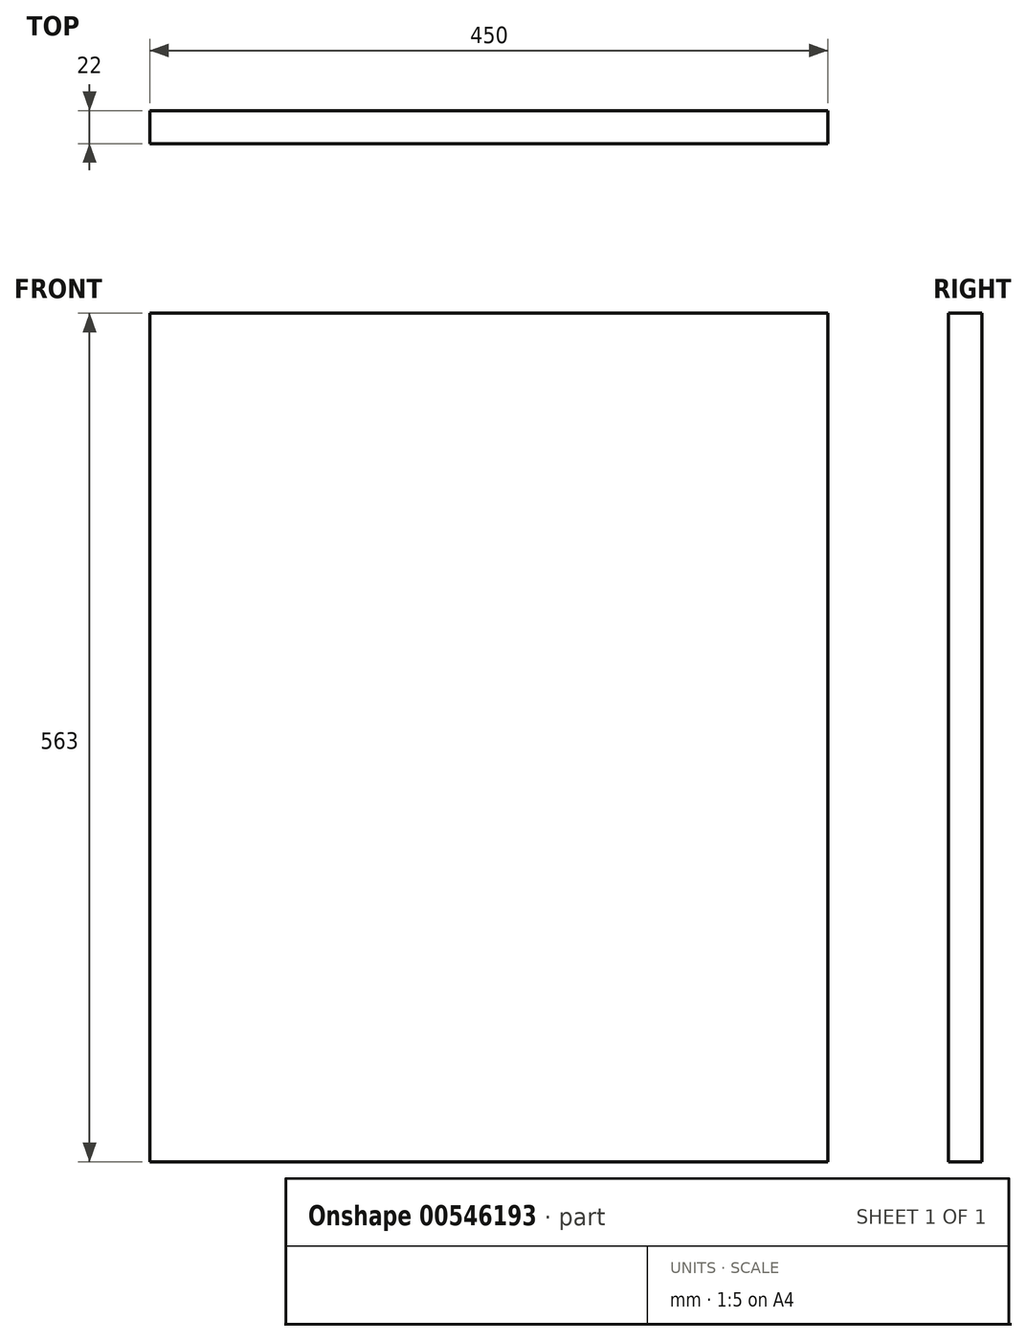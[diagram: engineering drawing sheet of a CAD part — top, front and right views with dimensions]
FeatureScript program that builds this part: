
annotation { "Feature Type Name" : "Feature", "Feature Type Description" : "" }
export const myFeature = defineFeature(function(context is Context, id is Id, definition is map)
    precondition{}
    {
        {
            var Q0;
            Q0=qCreatedBy(makeId("Top.planeOp"),FACE);
            var sketch = newSketch(context, id + "F0", { "sketchPlane" : qUnion([Q0])});
            skLineSegment(sketch, "E0.bottom", {"start": v(0, 0) * mm, "end": v(-450, 0) * mm});
            skLineSegment(sketch, "E0.top", {"start": v(0, 22) * mm, "end": v(-450, 22) * mm});
            skLineSegment(sketch, "E0.left", {"start": v(0, 0) * mm, "end": v(0, 22) * mm});
            skLineSegment(sketch, "E0.right", {"start": v(-450, 0) * mm, "end": v(-450, 22) * mm});
            skSolve(sketch);
        }
        {
            var Q0;
            Q0 = qSketchRegion(id + "F0", true);
            extrude(context, id + "F1", {"entities" : qUnion([Q0]), "depth" : 563 * mm, "offsetDistance" : 25 * mm});
        }
    });
